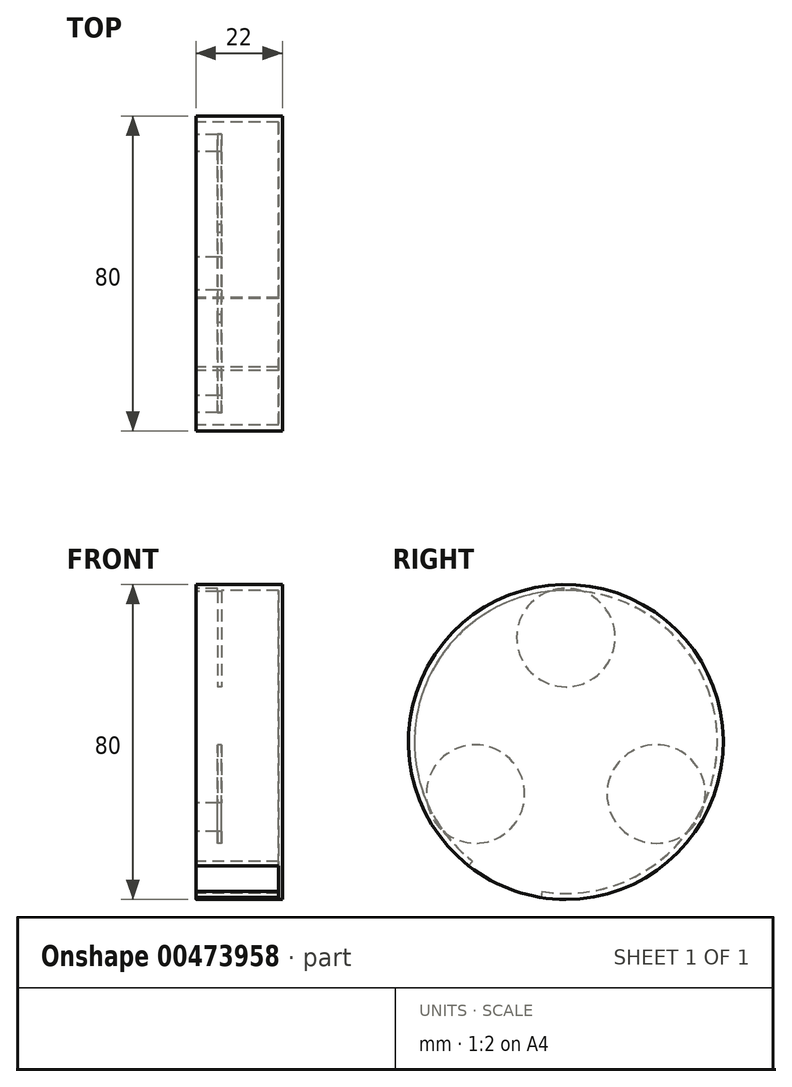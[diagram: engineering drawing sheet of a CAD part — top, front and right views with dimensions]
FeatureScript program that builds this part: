
annotation { "Feature Type Name" : "Feature", "Feature Type Description" : "" }
export const myFeature = defineFeature(function(context is Context, id is Id, definition is map)
    precondition{}
    {
        {
            var Q0;
            Q0=qCreatedBy(makeId("Right.planeOp"),FACE);
            var sketch = newSketch(context, id + "F0", { "sketchPlane" : qUnion([Q0])});
            skCircle(sketch, "E0", {"center": v(0, 0) * mm, "radius": 40 * mm});
            skSolve(sketch);
        }
        {
            var Q0;
            Q0=makeQuery(id+"F0.imprint","IMPRINT",FACE,{"disambiguationData":[TD([[makeQuery(id+"F0.imprint","IMPRINT",EDGE,{"derivedFrom":sQuery(id+"F0.wireOp",EDGE,"E0")}),1.0]])]});
            extrude(context, id + "F1", {"entities" : qUnion([Q0]), "depth" : 22 * mm, "offsetDistance" : 25 * mm});
        }
        {
            var Q0;
            Q0=makeQuery(id+"F1.opExtrude","CAP_FACE",FACE,{"disambiguationData":[OSD([sQuery(id+"F0.wireOp",EDGE,"E0")])],"isStart":true});
            shell(context, id + "F2", {"entities" : qUnion([Q0]), "thickness" : 1.5 * mm});
        }
        {
            var Q0;
            Q0=qCreatedBy(makeId("Right.planeOp"),FACE);
            var sketch = newSketch(context, id + "F3", { "sketchPlane" : qUnion([Q0])});
            skCircle(sketch, "E1.0", {"center": v(0, 0) * mm, "radius": 40 * mm});
            skCircle(sketch, "E2", {"center": v(0, 26.5) * mm, "radius": 12.5 * mm});
            skCircle(sketch, "E3", {"center": v(-22.95, -13.25) * mm, "radius": 12.5 * mm});
            skCircle(sketch, "E4", {"center": v(22.95, -13.25) * mm, "radius": 12.5 * mm});
            skSolve(sketch);
        }
        {
            var Q0;
            Q0=makeQuery(id+"F3.imprint","IMPRINT",FACE,{"disambiguationData":[TD([[makeQuery(id+"F3.imprint","IMPRINT",EDGE,{"derivedFrom":sQuery(id+"F3.wireOp",EDGE,"E4")}),1.0]])]});
            var Q1;
            Q1=makeQuery(id+"F3.imprint","IMPRINT",FACE,{"disambiguationData":[TD([[makeQuery(id+"F3.imprint","IMPRINT",EDGE,{"derivedFrom":sQuery(id+"F3.wireOp",EDGE,"E2")}),1.0]])]});
            var Q2;
            Q2=makeQuery(id+"F3.imprint","IMPRINT",FACE,{"disambiguationData":[TD([[makeQuery(id+"F3.imprint","IMPRINT",EDGE,{"derivedFrom":sQuery(id+"F3.wireOp",EDGE,"E3")}),1.0]])]});
            extrude(context, id + "F4", {"entities" : qUnion([Q0, Q1, Q2]), "operationType" : NewBodyOperationType.ADD, "depth" : 6.5 * mm, "offsetDistance" : 25 * mm});
        }
        {
            var Q0;
            Q0=qCreatedBy(makeId("Right.planeOp"),FACE);
            var sketch = newSketch(context, id + "F5", { "sketchPlane" : qUnion([Q0])});
            skCircle(sketch, "E5.0", {"center": v(0, 0) * mm, "radius": 40 * mm});
            skArc(sketch, "E6.0", {"start": v(-31.04, -22.78) * mm, "mid": v(0, -38.5) * mm, "end": v(31.04, -22.78) * mm});
            skLineSegment(sketch, "E7", {"start": v(0, 0) * mm, "end": v(-24.68, -31.48) * mm});
            skLineSegment(sketch, "E8", {"start": v(0, 0) * mm, "end": v(-6.36, -39.5) * mm});
            skSolve(sketch);
        }
        {
            var Q0;
            {var subQ0=sQuery(id+"F5.wireOp",EDGE,"E7");var subQ1=sQuery(id+"F5.wireOp",EDGE,"E5.0");var subQ2=makeQuery(id+"F5.imprint","INTERSECT",VERTEX,{"derivedFrom":[subQ1,subQ0]});Q0=makeQuery(id+"F5.imprint","IMPRINT",FACE,{"disambiguationData":[TD([[makeQuery(id+"F5.imprint","IMPRINT",EDGE,{"disambiguationData":[TD([[subQ2,-1.0]])],"derivedFrom":subQ1}),1.0]])]});}
            extrude(context, id + "F6", {"entities" : qUnion([Q0]), "operationType" : NewBodyOperationType.REMOVE, "depth" : 20.5 * mm, "offsetDistance" : 25 * mm});
        }
        {
            var Q0;
            Q0=makeQuery(id+"F4.boolean.opBoolean","MERGE",FACE,{"derivedFrom":[makeQuery(id+"F1.opExtrude","CAP_FACE",FACE,{"disambiguationData":[OSD([sQuery(id+"F0.wireOp",EDGE,"E0")])],"isStart":true}),makeQuery(id+"F4.opExtrude","CAP_FACE",FACE,{"disambiguationData":[OSD([sQuery(id+"F3.wireOp",EDGE,"E2")])],"isStart":true}),makeQuery(id+"F4.opExtrude","CAP_FACE",FACE,{"disambiguationData":[OSD([sQuery(id+"F3.wireOp",EDGE,"E3")])],"isStart":true}),makeQuery(id+"F4.opExtrude","CAP_FACE",FACE,{"disambiguationData":[OSD([sQuery(id+"F3.wireOp",EDGE,"E4")])],"isStart":true})]});
            var sketch = newSketch(context, id + "F7", { "sketchPlane" : qUnion([Q0])});
            skArc(sketch, "E9.0", {"start": v(-35.25, -15.49) * mm, "mid": v(-12.12, -7) * mm, "end": v(-31.04, -22.78) * mm});
            skArc(sketch, "E10.0", {"start": v(31.04, -22.78) * mm, "mid": v(12.12, -7) * mm, "end": v(35.25, -15.49) * mm});
            skArc(sketch, "E11.0", {"start": v(4.21, 38.27) * mm, "mid": v(0, 14) * mm, "end": v(-4.21, 38.27) * mm});
            skCircle(sketch, "E12", {"center": v(-22.95, -13.25) * mm, "radius": 12.5 * mm});
            skCircle(sketch, "E13", {"center": v(22.95, -13.25) * mm, "radius": 12.5 * mm});
            skCircle(sketch, "E14", {"center": v(0, 26.5) * mm, "radius": 12.5 * mm});
            skSolve(sketch);
        }
        {
            var Q0;
            Q0=makeQuery(id+"F7.imprint","IMPRINT",FACE,{"disambiguationData":[TD([[makeQuery(id+"F7.imprint","IMPRINT",EDGE,{"derivedFrom":sQuery(id+"F7.wireOp",EDGE,"E12")}),1.0]])]});
            var Q1;
            Q1=makeQuery(id+"F7.imprint","IMPRINT",FACE,{"disambiguationData":[TD([[makeQuery(id+"F7.imprint","IMPRINT",EDGE,{"derivedFrom":sQuery(id+"F7.wireOp",EDGE,"E13")}),1.0]])]});
            var Q2;
            Q2=makeQuery(id+"F7.imprint","IMPRINT",FACE,{"disambiguationData":[TD([[makeQuery(id+"F7.imprint","IMPRINT",EDGE,{"derivedFrom":sQuery(id+"F7.wireOp",EDGE,"E14")}),1.0]])]});
            extrude(context, id + "F8", {"entities" : qUnion([Q0, Q1, Q2]), "operationType" : NewBodyOperationType.REMOVE, "oppositeDirection" : true, "depth" : 5.5 * mm, "offsetDistance" : 25 * mm});
        }
        {
            var Q0;
            {var subQ0=sQuery(id+"F0.wireOp",EDGE,"E0");Q0=makeQuery(id+"F6.boolean.opBoolean","MERGE",FACE,{"derivedFrom":[makeQuery(id+"F2.opShell","OFFSET_FACE",FACE,{"disambiguationData":[OSD([subQ0]),TDD([makeQuery(id+"F1.opExtrude","CAP_FACE",FACE,{"disambiguationData":[OSD([subQ0])],"isStart":false})])]})],"fromTools":[makeQuery(id+"F6.opExtrude","CAP_FACE",FACE,{"disambiguationData":[OSD([sQuery(id+"F5.wireOp",EDGE,"E5.0"),sQuery(id+"F5.wireOp",EDGE,"E6.0"),sQuery(id+"F5.wireOp",EDGE,"E7"),sQuery(id+"F5.wireOp",EDGE,"E8")])],"isStart":false})]});}
            extrude(context, id + "F9", {"entities" : qUnion([Q0]), "operationType" : NewBodyOperationType.REMOVE, "oppositeDirection" : true, "depth" : 0.5 * mm, "offsetDistance" : 25 * mm});
        }
    });
